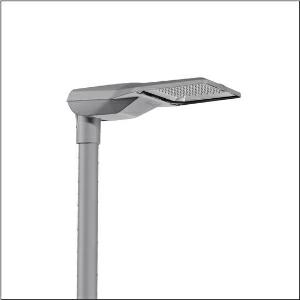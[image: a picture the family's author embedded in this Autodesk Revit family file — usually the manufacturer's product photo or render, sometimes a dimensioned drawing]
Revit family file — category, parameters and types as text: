
# Revit family: streetlight_sl_21_iq_midi___pc-r_5xe3g41g08mb_0911
name_source: partatom
category: Lighting Fixtures
units: mm (PartAtom-declared; Revit-internal decimal feet)

## family parameters
Cut with Voids When Loaded = No
Host = Face
Light Source = No
Part Type = Normal
Room Calculation Point = No
Round Connector Dimension = Use Diameter
Shared = No

## types (1)
- --- (1 x LED, 19370 lm, 146.7 W, 4000K)
    Apparent Load = 147 VA
    CIE Flux Codes = 38 78 98 100 100
    Color Rendering = 70
    Color Temperature = 4000K
    Default Elevation = 1800 mm
    Description = Streetlight SL 21 iQ midi, mast luminaire, primary light control with lens, of PMMA, primary optical cover: cover, of toughened safety glass, transparent, light distribution: PC-R, light emission: direct distribution, primary light characteristic: asymmetric, right, installation type: post-top, side-entry, LED, High Power LED, rated luminous flux: 19.370lm, luminous efficacy: 132lm/W, light colour: 740, colour temperature: 4000K, control: Street-Remote, Auto-Match, Temp-Guard, Lumen-Switch, Night-Set, Smart-Wire, Light-Fading, Desk-Remote (wireless, voltage-free reading and setting of iQ features in the workshop via application-optimized NFC function/RFID function), optimised constant luminous flux control (CLO 2.0), pre-setting: linear dimming characteristic, mains connection: 230..240V, AC, 50/60Hz, start of lifetime: 147W, end of service life: 161W, reduction: 62W, luminaire housing, of diecast aluminium, powder-coated, Siteco® metallic grey (DB 702S), corrosivity category C5 mid according to DIN EN ISO 12944, please order mast flange separately, inclination adjustable: 0°, 5°, 10°, 15°, sealing non-destructively replaceable, multi-level sealing system, length: 644mm, width: 335mm, height: 110mm, mast flange for spigot size: 42mm (side-entry): 5XC10008XM4, 60/48mm (side-entry/post-top): 5XC10108XM2, 76/60mm (side-entry/post-top): 5XC10108XM1, protection rating (complete): IP66, insulation class (complete): insulation class II (safety insulation), certification: CE, ENEC, ENEC+, VDE, impact resistance: IK09, permissible operating ambient temperature for outdoor applications: -40..+50°C, standard-compliant lighting for roads and squares, packaging unit: 1 piece

Light Distribution: PC-R
    Height = 111 mm
    Lamp = 1 x LED
    Lamp Light Flux = 19370 lm
    Lamp Power = 146.7 W
    Lamp count = 1
    Length = 644 mm
    Luminous efficacy = 132 lm/W
    Manufacturer = Siteco
    ModVariant = No
    Model = 5XE3G41G08MB
    Number of Poles = 1
    OnlyDefault = Yes
    Power Factor = 1
    Product Name = Streetlight SL 21 iQ midi | PC-R
    Product group = mast luminaire | pylon top
    ProductGroupID = 6100
    Protection Class = Protection class II
    Protection Degree = IP 66
    RLX_Detail_Level = 1
    RLX_Emergency_Light_Flux = 0 lm
    RLX_Emergency_Type = 0
    RLX_Emergency_Type_DB = No
    RlxData = <blob elided: 93077 chars, md5=24388cee>
    Socket = socket
    Standby Power = 0 W
    System Light Flux = 19370 lm
    System Power = 147 W
    Type Comments = factory setting: luminous flux: 100 % | dim-lin: 254 | 753 mA
    Type Image = l_1004298.jpg
    URL = http://relux.com
    VarID = @adj_032193
    Voltage = 0 V
    Weight = 0.00 kg
    Width = 336 mm

## geometry (parser evidence)
native form markers: Blend x4, Sweep x8
no freeform markers — native parametric forms only
